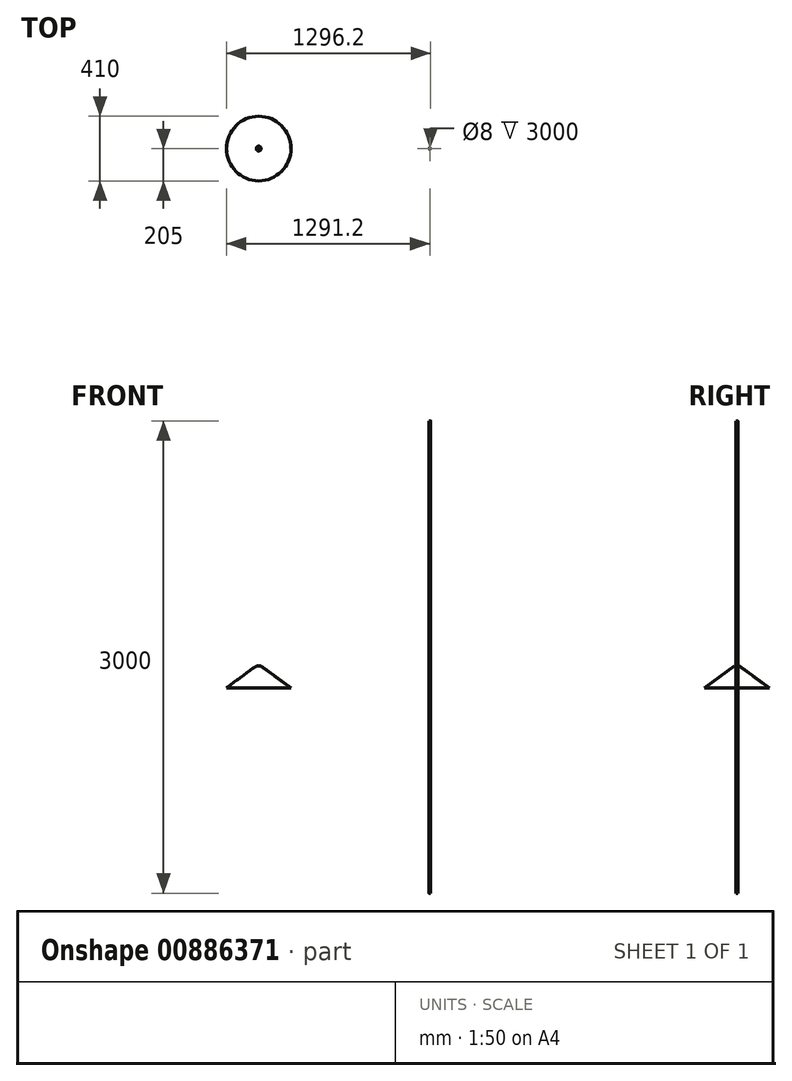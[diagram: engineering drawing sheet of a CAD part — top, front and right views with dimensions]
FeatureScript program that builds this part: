
annotation { "Feature Type Name" : "Feature", "Feature Type Description" : "" }
export const myFeature = defineFeature(function(context is Context, id is Id, definition is map)
    precondition{}
    {
        {
            var Q0;
            Q0=qCreatedBy(makeId("Front.planeOp"),FACE);
            var sketch = newSketch(context, id + "F0", { "sketchPlane" : qUnion([Q0])});
            skLineSegment(sketch, "E0", {"start": v(0, 0) * mm, "end": v(0, 140) * mm});
            skLineSegment(sketch, "E1", {"start": v(0, 140) * mm, "end": v(-15, 140) * mm});
            skLineSegment(sketch, "E2", {"start": v(-15, 140) * mm, "end": v(-205, 0) * mm});
            skLineSegment(sketch, "E3", {"start": v(-205, 0) * mm, "end": v(0, 0) * mm});
            skSolve(sketch);
        }
        {
            var Q0;
            Q0 = qSketchRegion(id + "F0", true);
            var Q1;
            Q1=sQuery(id+"F0.wireOp",EDGE,"E0");
            revolve(context, id + "F1", {"surfaceOperationType" : NewSurfaceOperationType.NEW, "entities" : qUnion([Q0]), "axis" : qUnion([Q1]), "revolveType" : RevolveType.FULL});
        }
        {
            var Q0;
            Q0=qCreatedBy(makeId("Front.planeOp"),FACE);
            var sketch = newSketch(context, id + "F2", { "sketchPlane" : qUnion([Q0])});
            skLineSegment(sketch, "E4", {"start": v(-200, 0) * mm, "end": v(-5, 140) * mm});
            skLineSegment(sketch, "E5", {"start": v(0, 140) * mm, "end": v(0, 0) * mm});
            skLineSegment(sketch, "E6", {"start": v(0, 0) * mm, "end": v(-200, 0) * mm});
            skLineSegment(sketch, "E7", {"start": v(-5, 140) * mm, "end": v(0, 140) * mm});
            skSolve(sketch);
        }
        {
            var Q0;
            Q0 = qSketchRegion(id + "F2", true);
            var Q1;
            Q1=sQuery(id+"F2.wireOp",EDGE,"E5");
            revolve(context, id + "F3", {"operationType" : NewBodyOperationType.REMOVE, "surfaceOperationType" : NewSurfaceOperationType.NEW, "entities" : qUnion([Q0]), "axis" : qUnion([Q1]), "revolveType" : RevolveType.FULL, "oppositeDirection" : true});
        }
        {
            var Q0;
            Q0=qCreatedBy(makeId("Front.planeOp"),FACE);
            var sketch = newSketch(context, id + "F4", { "sketchPlane" : qUnion([Q0])});
            skLineSegment(sketch, "E8", {"start": v(1091.2, 1695.37) * mm, "end": v(1091.2, -1304.63) * mm});
            skLineSegment(sketch, "E9", {"start": v(1091.2, -1304.63) * mm, "end": v(1086.2, -1304.63) * mm});
            skLineSegment(sketch, "E10", {"start": v(1086.2, -1304.63) * mm, "end": v(1086.2, 1695.37) * mm});
            skLineSegment(sketch, "E11", {"start": v(1086.2, 1695.37) * mm, "end": v(1091.2, 1695.37) * mm});
            skSolve(sketch);
        }
        {
            var Q0;
            Q0 = qSketchRegion(id + "F4", true);
            var Q1;
            Q1=sQuery(id+"F4.wireOp",EDGE,"E10");
            revolve(context, id + "F5", {"surfaceOperationType" : NewSurfaceOperationType.NEW, "entities" : qUnion([Q0]), "axis" : qUnion([Q1]), "revolveType" : RevolveType.FULL});
        }
        {
            var Q0;
            Q0=qCreatedBy(makeId("Front.planeOp"),FACE);
            var sketch = newSketch(context, id + "F6", { "sketchPlane" : qUnion([Q0])});
            skLineSegment(sketch, "E12", {"start": v(1090.2, -1304.63) * mm, "end": v(1086.2, -1304.63) * mm});
            skLineSegment(sketch, "E13", {"start": v(1090.2, -1304.63) * mm, "end": v(1090.2, 1695.37) * mm});
            skLineSegment(sketch, "E14", {"start": v(1090.2, 1695.37) * mm, "end": v(1086.2, 1695.37) * mm});
            skLineSegment(sketch, "E15", {"start": v(1086.2, 1695.37) * mm, "end": v(1086.2, -1304.63) * mm});
            skSolve(sketch);
        }
        {
            var Q0;
            Q0 = qSketchRegion(id + "F6", true);
            var Q1;
            Q1=sQuery(id+"F6.wireOp",EDGE,"E15");
            revolve(context, id + "F7", {"operationType" : NewBodyOperationType.REMOVE, "surfaceOperationType" : NewSurfaceOperationType.NEW, "entities" : qUnion([Q0]), "axis" : qUnion([Q1]), "revolveType" : RevolveType.FULL, "oppositeDirection" : true});
        }
    });
